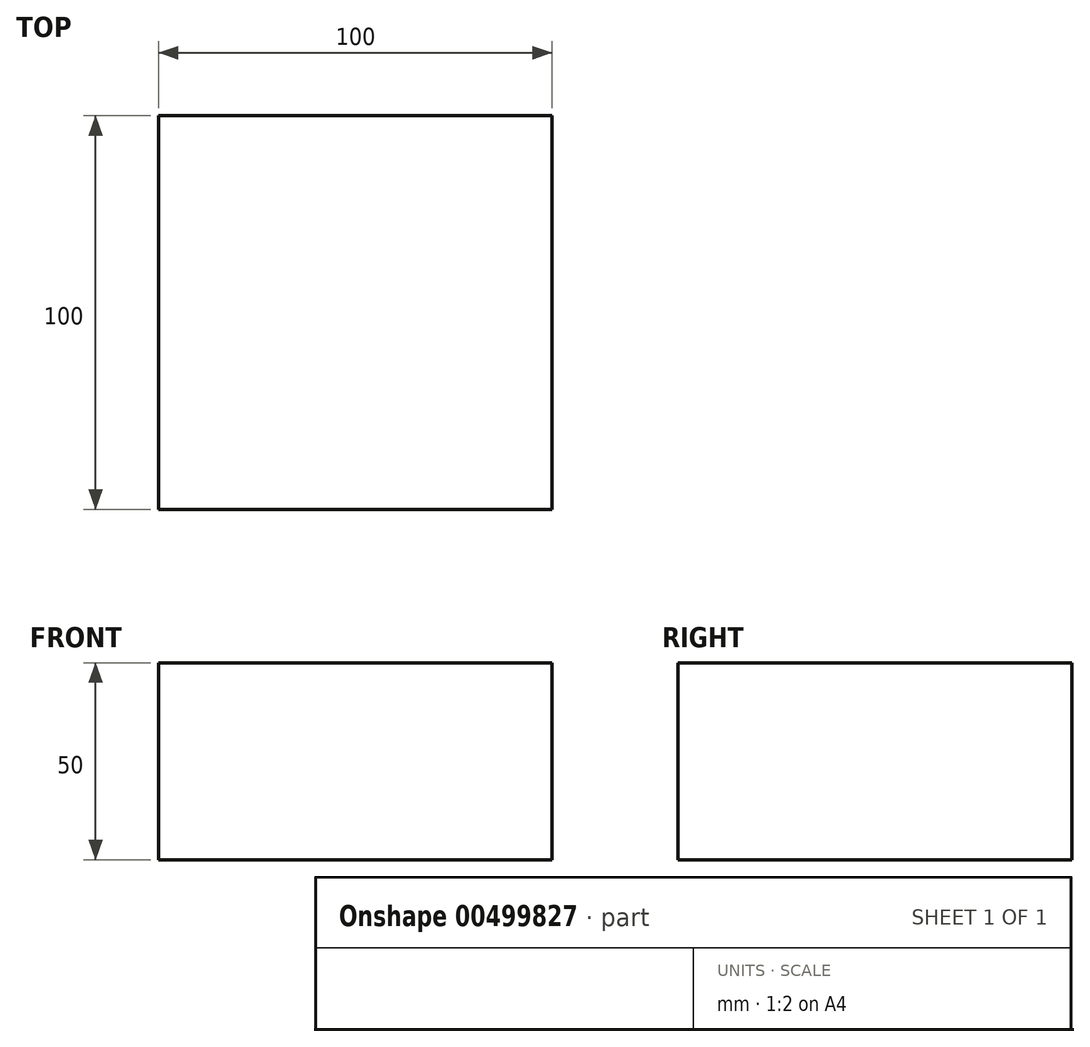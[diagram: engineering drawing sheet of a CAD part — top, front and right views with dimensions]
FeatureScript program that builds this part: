
annotation { "Feature Type Name" : "Feature", "Feature Type Description" : "" }
export const myFeature = defineFeature(function(context is Context, id is Id, definition is map)
    precondition{}
    {
        {
            var Q0;
            Q0=qCreatedBy(makeId("Front.planeOp"),FACE);
            var sketch = newSketch(context, id + "F0", { "sketchPlane" : qUnion([Q0])});
            skLineSegment(sketch, "E0.bottom", {"start": v(50, 25) * mm, "end": v(-50, 25) * mm});
            skLineSegment(sketch, "E0.top", {"start": v(50, -25) * mm, "end": v(-50, -25) * mm});
            skLineSegment(sketch, "E0.left", {"start": v(50, 25) * mm, "end": v(50, -25) * mm});
            skLineSegment(sketch, "E0.right", {"start": v(-50, 25) * mm, "end": v(-50, -25) * mm});
            skPoint(sketch, "E0.middle", {"position": v(0, 0) * mm});
            skSolve(sketch);
        }
        {
            var Q0;
            Q0=qSketchRegion(id+"F0",true);
            extrude(context, id + "F1", {"entities" : qUnion([Q0]), "depth" : 100 * mm, "symmetric" : true});
        }
    });
